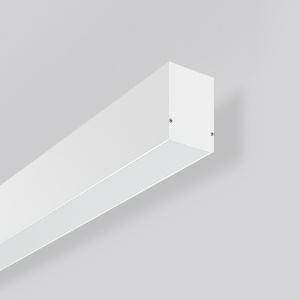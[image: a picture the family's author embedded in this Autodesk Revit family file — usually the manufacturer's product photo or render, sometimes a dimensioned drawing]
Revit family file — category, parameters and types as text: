
# Revit family: less_is_more_50_312612_002_0b17
name_source: partatom
category: Lighting Fixtures
units: mm (PartAtom-declared; Revit-internal decimal feet)

## family parameters
Cut with Voids When Loaded = No
Host = Face
Light Source = No
Part Type = Normal
Room Calculation Point = No
Round Connector Dimension = Use Diameter
Shared = No

## types (1)
- LESS IS MORE 50 (1 x LED Modul 830, 3900 lm, 3000)
    Apparent Load = 30 VA
    CIE Flux Codes = 48 80 96 50 100
    Color Rendering = 80
    Color Temperature = 3000
    Default Elevation = 1800 mm
    Description = Series: LESS IS MORE 50
Linear wall luminaires. Housing: extruded aluminium profile, powder-coated. End cap aluminium powder-coated. Diffuser made of non-yellowing plastic (PMMA), opal. Direct 50%, indirect 50% light emission. Suitable for Wall (surface). LED unit with integrated converter interchangeable and removable. Suitable for through-wiring. With sensors or as a safety luminaire on request. 
Colour: traffic white, matt (RAL 9016)
Length: 1687 mm
Width: 67 mm
Height: 75 mm
Lamp: LED
Socket: without socket
Colour temperature: 3000K
Colour rendering index (CRI): 80
Light source: LED
Socket lamp2: Without base
Colour temperature: 3000K
Colour rendering index (CRI) 2: 80
System power: 30 W
Rated luminous flux: 3900 lm
Luminous efficiency: 130 lm/W
Control gear: Regulated power supply
Control gear: Regulated power supply
Protection class: I
Type of protection: IP 20
    Height = 75 mm
    Lamp = 1 x LED Modul 830
    Lamp Light Flux = 3900 lm
    Lamp count = 1
    Length = 1687 mm
    Lifetime = 50000 h
    Luminous efficacy = 130 lm/W
    Manufacturer = RZB
    ModVariant = No
    Model = 312612.002
    Mounting Place = Wall
    Mounting Type = Surface mounted
    Number of Poles = 1
    OnlyDefault = Yes
    Power Factor = 1
    Product Name = LESS IS MORE 50
    Product group = Surface mounted LED linear luminaires
    ProductGroupID = 2007
    Protection Class = Protection class I
    Protection Degree = IP 20
    RLX_Detail_Level = 1
    RLX_Emergency_Light_Flux = 0 lm
    RLX_Emergency_Type = 0
    RLX_Emergency_Type_DB = No
    RlxData = <blob elided: 39645 chars, md5=a428d0ed>
    Socket = socket
    Standby Power = 0 W
    System Light Flux = 3900 lm
    System Power = 30 W
    Type Comments = Product without accessories
    Type Image = 312606.002.jpg
    URL = http://relux.com
    VarID = ---
    Voltage = 0 V
    Weight = 0.00 kg
    Width = 67 mm

## geometry (parser evidence)
native form markers: Blend x4, Sweep x12
no freeform markers — native parametric forms only
